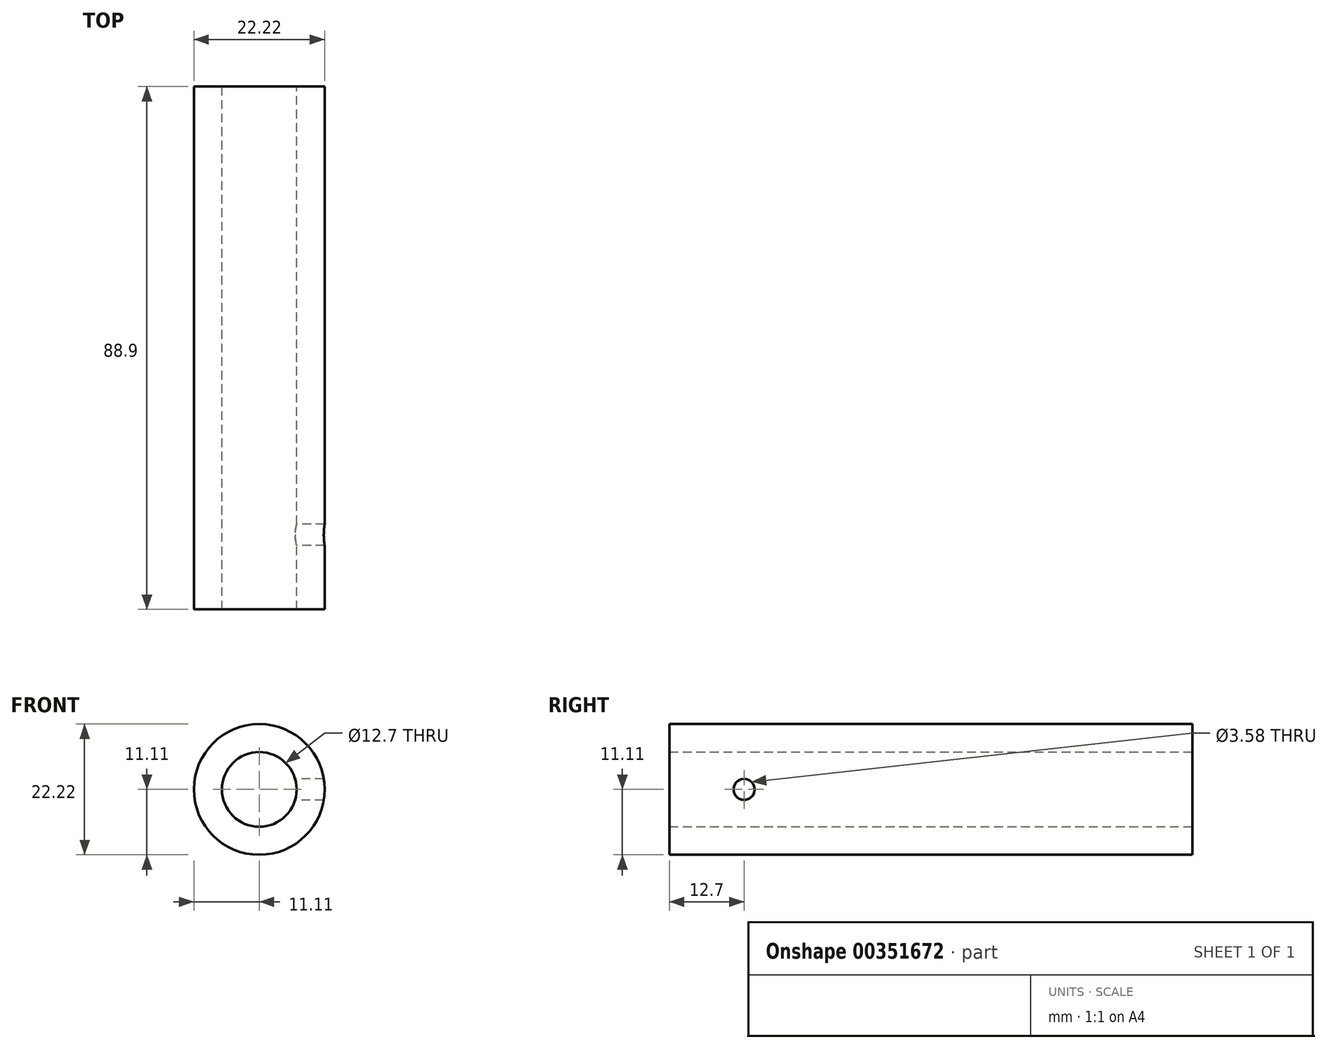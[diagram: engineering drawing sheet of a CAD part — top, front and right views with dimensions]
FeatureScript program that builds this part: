
annotation { "Feature Type Name" : "Feature", "Feature Type Description" : "" }
export const myFeature = defineFeature(function(context is Context, id is Id, definition is map)
    precondition{}
    {
        {
            var Q0;
            Q0=qCreatedBy(makeId("Front.planeOp"),FACE);
            var sketch = newSketch(context, id + "F0", { "sketchPlane" : qUnion([Q0])});
            skCircle(sketch, "E0", {"center": v(0, 0) * mm, "radius": 11.11 * mm});
            skCircle(sketch, "E1", {"center": v(0, 0) * mm, "radius": 6.35 * mm});
            skSolve(sketch);
        }
        {
            var Q0;
            Q0=makeQuery(id+"F0.imprint","IMPRINT",FACE,{"disambiguationData":[TD([[makeQuery(id+"F0.imprint","IMPRINT",EDGE,{"derivedFrom":sQuery(id+"F0.wireOp",EDGE,"E0")}),1.0]])]});
            extrude(context, id + "F1", {"entities" : qUnion([Q0]), "endBound" : BoundingType.SYMMETRIC, "depth" : 88.9 * mm});
        }
        {
            var Q0;
            Q0=qCreatedBy(makeId("Right.planeOp"),FACE);
            var sketch = newSketch(context, id + "F2", { "sketchPlane" : qUnion([Q0])});
            skCircle(sketch, "E2", {"center": v(-31.75, 0) * mm, "radius": 1.8 * mm});
            skSolve(sketch);
        }
        {
            var Q0;
            Q0 = qSketchRegion(id + "F2", true);
            extrude(context, id + "F3", {"entities" : qUnion([Q0]), "operationType" : NewBodyOperationType.REMOVE, "depth" : 12.7 * mm});
        }
    });
